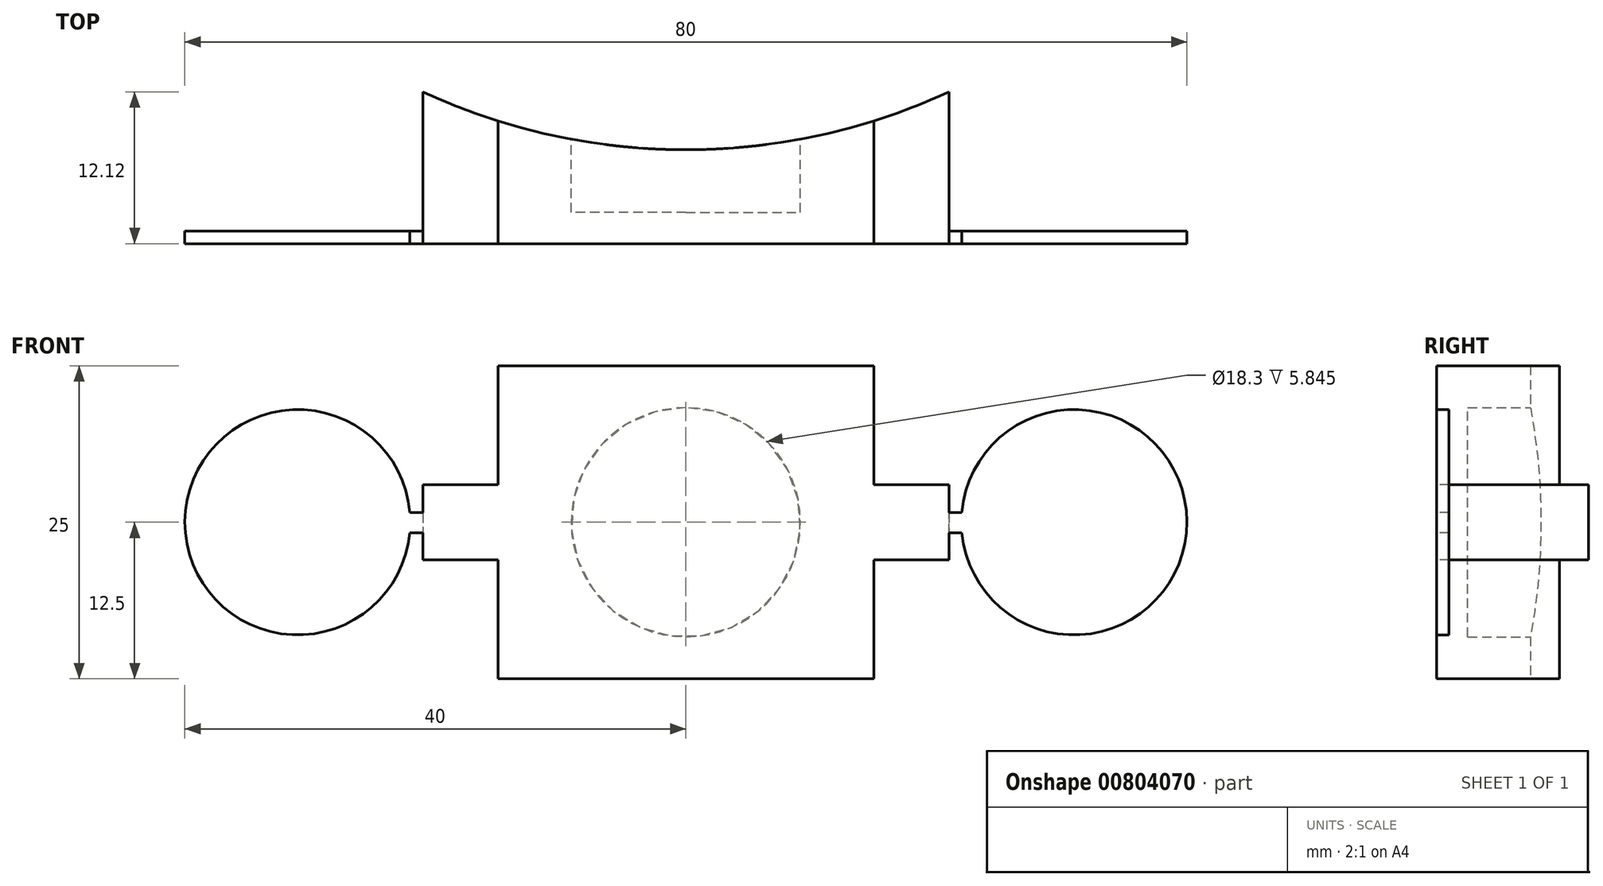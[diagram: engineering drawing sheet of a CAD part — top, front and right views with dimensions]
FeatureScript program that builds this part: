
annotation { "Feature Type Name" : "Feature", "Feature Type Description" : "" }
export const myFeature = defineFeature(function(context is Context, id is Id, definition is map)
    precondition{}
    {
        {
            var Q0;
            Q0=qCreatedBy(makeId("Top.planeOp"),FACE);
            var sketch = newSketch(context, id + "F0", { "sketchPlane" : qUnion([Q0])});
            skArc(sketch, "E0", {"start": v(-50, 0) * mm, "mid": v(0, -50) * mm, "end": v(50, 0) * mm});
            skArc(sketch, "E1", {"start": v(-55, 0) * mm, "mid": v(0, -55) * mm, "end": v(55, 0) * mm});
            skLineSegment(sketch, "E2", {"start": v(-55, 0) * mm, "end": v(-50, 0) * mm});
            skLineSegment(sketch, "E3.trimOffspring", {"start": v(50, 0) * mm, "end": v(55, 0) * mm});
            skSolve(sketch);
        }
        {
            var Q0;
            Q0=qSketchRegion(id+"F0",true);
            extrude(context, id + "F1", {"entities" : qUnion([Q0]), "endBound" : BoundingType.SYMMETRIC, "depth" : 25 * mm, "offsetDistance" : 25 * mm});
        }
        {
            var Q0;
            Q0=makeQuery(id+"F1.opExtrude","CAP_FACE",FACE,{"disambiguationData":[OSD([sQuery(id+"F0.wireOp",EDGE,"E0"),sQuery(id+"F0.wireOp",EDGE,"E1")])],"isStart":false});
            var sketch = newSketch(context, id + "F2", { "sketchPlane" : qUnion([Q0])});
            skLineSegment(sketch, "E4", {"start": v(-55, 0) * mm, "end": v(-55, -57.5) * mm});
            skLineSegment(sketch, "E5", {"start": v(55, 0) * mm, "end": v(55, -57.5) * mm});
            skLineSegment(sketch, "E6", {"start": v(0, -57.5) * mm, "end": v(55, -57.5) * mm});
            skLineSegment(sketch, "E7", {"start": v(0, -57.5) * mm, "end": v(-55, -57.5) * mm});
            skArc(sketch, "E8", {"start": v(-55, 0) * mm, "mid": v(0, -55) * mm, "end": v(55, 0) * mm});
            skLineSegment(sketch, "E9", {"start": v(0, -55) * mm, "end": v(0, -57.5) * mm, "construction": true});
            skSolve(sketch);
        }
        {
            var Q0;
            Q0=qSketchRegion(id+"F2",true);
            extrude(context, id + "F3", {"entities" : qUnion([Q0]), "operationType" : NewBodyOperationType.ADD, "oppositeDirection" : true, "depth" : 25 * mm, "offsetDistance" : 25 * mm});
        }
        {
            var Q0;
            Q0=qCreatedBy(makeId("Front.planeOp"),FACE);
            var sketch = newSketch(context, id + "F4", { "sketchPlane" : qUnion([Q0])});
            skCircle(sketch, "E10", {"center": v(0, 0) * mm, "radius": 9.15 * mm});
            skSolve(sketch);
        }
        {
            var Q0;
            Q0=qSketchRegion(id+"F4",true);
            extrude(context, id + "F5", {"entities" : qUnion([Q0]), "operationType" : NewBodyOperationType.REMOVE, "depth" : 55 * mm, "offsetDistance" : 25 * mm});
        }
        {
            var Q0;
            Q0=qCreatedBy(makeId("Right.planeOp"),FACE);
            var sketch = newSketch(context, id + "F6", { "sketchPlane" : qUnion([Q0])});
            skLineSegment(sketch, "E11", {"start": v(0, 0) * mm, "end": v(-11, 0) * mm, "construction": true});
            skCircle(sketch, "E12", {"center": v(-11, 0) * mm, "radius": 9.05 * mm});
            skSolve(sketch);
        }
        {
            var Q0;
            Q0=qSketchRegion(id+"F6",true);
            extrude(context, id + "F7", {"entities" : qUnion([Q0]), "operationType" : NewBodyOperationType.REMOVE, "endBound" : BoundingType.SYMMETRIC, "oppositeDirection" : true, "depth" : 105 * mm, "offsetDistance" : 25 * mm});
        }
        {
            var Q0;
            Q0=makeQuery(id+"F3.opExtrude","SWEPT_FACE",FACE,{"disambiguationData":[OSD([sQuery(id+"F2.wireOp",EDGE,"E6"),sQuery(id+"F2.wireOp",EDGE,"E7")])]});
            var sketch = newSketch(context, id + "F8", { "sketchPlane" : qUnion([Q0])});
            skLineSegment(sketch, "E13", {"start": v(55, 0) * mm, "end": v(65, 0) * mm, "construction": true});
            skLineSegment(sketch, "E14", {"start": v(-55, 0) * mm, "end": v(-65, 0) * mm, "construction": true});
            skArc(sketch, "E15", {"start": v(56.19, -1.83) * mm, "mid": v(74, 0.24) * mm, "end": v(56.1, 1.35) * mm});
            skArc(sketch, "E16", {"start": v(-56.02, 0.59) * mm, "mid": v(-74, -0.07) * mm, "end": v(-56.01, -0.44) * mm});
            skLineSegment(sketch, "E17", {"start": v(0, -12.5) * mm, "end": v(-55, -12.5) * mm, "construction": true});
            skLineSegment(sketch, "E18", {"start": v(-27.5, -12.5) * mm, "end": v(-27.5, -22.5) * mm, "construction": true});
            skLineSegment(sketch, "E19", {"start": v(0, -12.5) * mm, "end": v(55, -12.5) * mm, "construction": true});
            skLineSegment(sketch, "E20", {"start": v(27.5, -12.5) * mm, "end": v(27.5, -22.5) * mm, "construction": true});
            skLineSegment(sketch, "E21", {"start": v(-55, 12.5) * mm, "end": v(0, 12.5) * mm, "construction": true});
            skLineSegment(sketch, "E22", {"start": v(-27.5, 12.5) * mm, "end": v(-27.5, 22.5) * mm, "construction": true});
            skLineSegment(sketch, "E23", {"start": v(0, 12.5) * mm, "end": v(55, 12.5) * mm, "construction": true});
            skLineSegment(sketch, "E24", {"start": v(27.5, 12.5) * mm, "end": v(27.5, 22.5) * mm, "construction": true});
            skArc(sketch, "E25", {"start": v(26.67, -13.54) * mm, "mid": v(27.5, -31.5) * mm, "end": v(28.35, -13.54) * mm});
            skArc(sketch, "E26", {"start": v(-28.3, -13.54) * mm, "mid": v(-27.52, -31.5) * mm, "end": v(-26.66, -13.54) * mm});
            skArc(sketch, "E27", {"start": v(-26.33, 13.58) * mm, "mid": v(-27.67, 31.5) * mm, "end": v(-28.34, 13.54) * mm});
            skArc(sketch, "E28", {"start": v(28.64, 13.57) * mm, "mid": v(27.37, 31.5) * mm, "end": v(26.62, 13.54) * mm});
            skLineSegment(sketch, "E29", {"start": v(56.19, -1.83) * mm, "end": v(55, -1.83) * mm});
            skLineSegment(sketch, "E30", {"start": v(56.1, 1.35) * mm, "end": v(55, 1.35) * mm});
            skLineSegment(sketch, "E31", {"start": v(55, -1.83) * mm, "end": v(55, 1.35) * mm});
            skLineSegment(sketch, "E32", {"start": v(26.62, 13.54) * mm, "end": v(26.62, 12.5) * mm});
            skLineSegment(sketch, "E33", {"start": v(28.64, 13.57) * mm, "end": v(28.64, 12.5) * mm});
            skLineSegment(sketch, "E34", {"start": v(28.64, 12.5) * mm, "end": v(26.62, 12.5) * mm});
            skLineSegment(sketch, "E35", {"start": v(-28.34, 13.54) * mm, "end": v(-28.34, 12.5) * mm});
            skLineSegment(sketch, "E36", {"start": v(-26.33, 13.58) * mm, "end": v(-26.33, 12.5) * mm});
            skLineSegment(sketch, "E37", {"start": v(-26.33, 12.5) * mm, "end": v(-28.34, 12.5) * mm});
            skLineSegment(sketch, "E38", {"start": v(-56.02, 0.59) * mm, "end": v(-55, 0.59) * mm});
            skLineSegment(sketch, "E39", {"start": v(-56.01, -0.44) * mm, "end": v(-55, -0.44) * mm});
            skLineSegment(sketch, "E40", {"start": v(-55, -0.44) * mm, "end": v(-55, 0.59) * mm});
            skLineSegment(sketch, "E41", {"start": v(-28.3, -13.54) * mm, "end": v(-28.3, -12.5) * mm});
            skLineSegment(sketch, "E42", {"start": v(-26.66, -13.54) * mm, "end": v(-26.66, -12.5) * mm});
            skLineSegment(sketch, "E43", {"start": v(-26.66, -12.5) * mm, "end": v(-28.3, -12.5) * mm});
            skLineSegment(sketch, "E44", {"start": v(26.67, -13.54) * mm, "end": v(26.67, -12.5) * mm});
            skLineSegment(sketch, "E45", {"start": v(28.35, -13.54) * mm, "end": v(28.35, -12.5) * mm});
            skLineSegment(sketch, "E46", {"start": v(28.35, -12.5) * mm, "end": v(26.67, -12.5) * mm});
            skSolve(sketch);
        }
        {
            var Q0;
            Q0=qSketchRegion(id+"F8",true);
            extrude(context, id + "F9", {"entities" : qUnion([Q0]), "operationType" : NewBodyOperationType.ADD, "oppositeDirection" : true, "depth" : 3 * mm, "offsetDistance" : 25 * mm});
        }
        {
            var Q0;
            Q0=makeQuery(id+"F9.boolean.opBoolean","MERGE",FACE,{"derivedFrom":[makeQuery(id+"F3.opExtrude","SWEPT_FACE",FACE,{"disambiguationData":[OSD([sQuery(id+"F2.wireOp",EDGE,"E6"),sQuery(id+"F2.wireOp",EDGE,"E7")])]}),makeQuery(id+"F9.opExtrude","CAP_FACE",FACE,{"disambiguationData":[OSD([sQuery(id+"F8.wireOp",EDGE,"E15"),sQuery(id+"F8.wireOp",EDGE,"E29"),sQuery(id+"F8.wireOp",EDGE,"E30"),sQuery(id+"F8.wireOp",EDGE,"E31")])],"isStart":true}),makeQuery(id+"F9.opExtrude","CAP_FACE",FACE,{"disambiguationData":[OSD([sQuery(id+"F8.wireOp",EDGE,"E16"),sQuery(id+"F8.wireOp",EDGE,"E38"),sQuery(id+"F8.wireOp",EDGE,"E39"),sQuery(id+"F8.wireOp",EDGE,"E40")])],"isStart":true}),makeQuery(id+"F9.opExtrude","CAP_FACE",FACE,{"disambiguationData":[OSD([sQuery(id+"F8.wireOp",EDGE,"E25"),sQuery(id+"F8.wireOp",EDGE,"E44"),sQuery(id+"F8.wireOp",EDGE,"E45"),sQuery(id+"F8.wireOp",EDGE,"E46")])],"isStart":true}),makeQuery(id+"F9.opExtrude","CAP_FACE",FACE,{"disambiguationData":[OSD([sQuery(id+"F8.wireOp",EDGE,"E26"),sQuery(id+"F8.wireOp",EDGE,"E41"),sQuery(id+"F8.wireOp",EDGE,"E42"),sQuery(id+"F8.wireOp",EDGE,"E43")])],"isStart":true}),makeQuery(id+"F9.opExtrude","CAP_FACE",FACE,{"disambiguationData":[OSD([sQuery(id+"F8.wireOp",EDGE,"E27"),sQuery(id+"F8.wireOp",EDGE,"E35"),sQuery(id+"F8.wireOp",EDGE,"E36"),sQuery(id+"F8.wireOp",EDGE,"E37")])],"isStart":true}),makeQuery(id+"F9.opExtrude","CAP_FACE",FACE,{"disambiguationData":[OSD([sQuery(id+"F8.wireOp",EDGE,"E28"),sQuery(id+"F8.wireOp",EDGE,"E32"),sQuery(id+"F8.wireOp",EDGE,"E33"),sQuery(id+"F8.wireOp",EDGE,"E34")])],"isStart":true})]});
            var sketch = newSketch(context, id + "F10", { "sketchPlane" : qUnion([Q0])});
            skLineSegment(sketch, "E47", {"start": v(0, 12.5) * mm, "end": v(0, -12.5) * mm, "construction": true});
            skLineSegment(sketch, "E48.left", {"start": v(-15, 12.5) * mm, "end": v(-15, 3) * mm});
            skLineSegment(sketch, "E48.right", {"start": v(15, 12.5) * mm, "end": v(15, 3) * mm});
            skLineSegment(sketch, "E49", {"start": v(15, 0) * mm, "end": v(0, 0) * mm, "construction": true});
            skLineSegment(sketch, "E50", {"start": v(0, 0) * mm, "end": v(-15, 0) * mm, "construction": true});
            skLineSegment(sketch, "E51", {"start": v(-15, 0) * mm, "end": v(-21, 0) * mm, "construction": true});
            skLineSegment(sketch, "E52", {"start": v(-21, 0) * mm, "end": v(-21, 3) * mm});
            skLineSegment(sketch, "E53", {"start": v(-21, 3) * mm, "end": v(-15, 3) * mm});
            skLineSegment(sketch, "E54", {"start": v(-21, 0) * mm, "end": v(-21, -3) * mm});
            skLineSegment(sketch, "E55", {"start": v(-21, -3) * mm, "end": v(-15, -3) * mm});
            skLineSegment(sketch, "E56.trimOffspring", {"start": v(-15, -3) * mm, "end": v(-15, -12.5) * mm});
            skLineSegment(sketch, "E57", {"start": v(15, 0) * mm, "end": v(21, 0) * mm, "construction": true});
            skLineSegment(sketch, "E58", {"start": v(21, 0) * mm, "end": v(21, 3) * mm});
            skLineSegment(sketch, "E59", {"start": v(21, 3) * mm, "end": v(15, 3) * mm});
            skLineSegment(sketch, "E60", {"start": v(21, 0) * mm, "end": v(21, -3) * mm});
            skLineSegment(sketch, "E61", {"start": v(21, -3) * mm, "end": v(15, -3) * mm});
            skLineSegment(sketch, "E62.trimOffspring", {"start": v(15, -3) * mm, "end": v(15, -12.5) * mm});
            skLineSegment(sketch, "E63", {"start": v(15, 12.5) * mm, "end": v(15, 42.1) * mm});
            skLineSegment(sketch, "E64", {"start": v(15, 42.1) * mm, "end": v(79.78, 42.1) * mm});
            skLineSegment(sketch, "E65", {"start": v(79.78, 42.1) * mm, "end": v(79.78, -47.12) * mm});
            skLineSegment(sketch, "E66", {"start": v(79.78, -47.12) * mm, "end": v(15, -47.12) * mm});
            skLineSegment(sketch, "E67", {"start": v(15, -47.12) * mm, "end": v(15, -12.5) * mm});
            skLineSegment(sketch, "E68", {"start": v(-15, 12.5) * mm, "end": v(-15, 43.2) * mm});
            skLineSegment(sketch, "E69", {"start": v(-15, 43.2) * mm, "end": v(-80.15, 43.2) * mm});
            skLineSegment(sketch, "E70", {"start": v(-80.15, 43.2) * mm, "end": v(-80.15, -41.9) * mm});
            skLineSegment(sketch, "E71", {"start": v(-80.15, -41.9) * mm, "end": v(-15, -41.9) * mm});
            skLineSegment(sketch, "E72", {"start": v(-15, -41.9) * mm, "end": v(-15, -12.5) * mm});
            skSolve(sketch);
        }
        {
            var Q0;
            Q0 = qSketchRegion(id + "F10", true);
            extrude(context, id + "F11", {"entities" : qUnion([Q0]), "operationType" : NewBodyOperationType.REMOVE, "endBound" : BoundingType.THROUGH_ALL, "oppositeDirection" : true, "depth" : 25 * mm, "offsetDistance" : 25 * mm});
        }
        {
            var Q0;
            Q0=makeQuery(id+"F9.boolean.opBoolean","MERGE",FACE,{"derivedFrom":[makeQuery(id+"F3.opExtrude","SWEPT_FACE",FACE,{"disambiguationData":[OSD([sQuery(id+"F2.wireOp",EDGE,"E6"),sQuery(id+"F2.wireOp",EDGE,"E7")])]}),makeQuery(id+"F9.opExtrude","CAP_FACE",FACE,{"disambiguationData":[OSD([sQuery(id+"F8.wireOp",EDGE,"E15"),sQuery(id+"F8.wireOp",EDGE,"E29"),sQuery(id+"F8.wireOp",EDGE,"E30"),sQuery(id+"F8.wireOp",EDGE,"E31")])],"isStart":true}),makeQuery(id+"F9.opExtrude","CAP_FACE",FACE,{"disambiguationData":[OSD([sQuery(id+"F8.wireOp",EDGE,"E16"),sQuery(id+"F8.wireOp",EDGE,"E38"),sQuery(id+"F8.wireOp",EDGE,"E39"),sQuery(id+"F8.wireOp",EDGE,"E40")])],"isStart":true}),makeQuery(id+"F9.opExtrude","CAP_FACE",FACE,{"disambiguationData":[OSD([sQuery(id+"F8.wireOp",EDGE,"E25"),sQuery(id+"F8.wireOp",EDGE,"E44"),sQuery(id+"F8.wireOp",EDGE,"E45"),sQuery(id+"F8.wireOp",EDGE,"E46")])],"isStart":true}),makeQuery(id+"F9.opExtrude","CAP_FACE",FACE,{"disambiguationData":[OSD([sQuery(id+"F8.wireOp",EDGE,"E26"),sQuery(id+"F8.wireOp",EDGE,"E41"),sQuery(id+"F8.wireOp",EDGE,"E42"),sQuery(id+"F8.wireOp",EDGE,"E43")])],"isStart":true}),makeQuery(id+"F9.opExtrude","CAP_FACE",FACE,{"disambiguationData":[OSD([sQuery(id+"F8.wireOp",EDGE,"E27"),sQuery(id+"F8.wireOp",EDGE,"E35"),sQuery(id+"F8.wireOp",EDGE,"E36"),sQuery(id+"F8.wireOp",EDGE,"E37")])],"isStart":true}),makeQuery(id+"F9.opExtrude","CAP_FACE",FACE,{"disambiguationData":[OSD([sQuery(id+"F8.wireOp",EDGE,"E28"),sQuery(id+"F8.wireOp",EDGE,"E32"),sQuery(id+"F8.wireOp",EDGE,"E33"),sQuery(id+"F8.wireOp",EDGE,"E34")])],"isStart":true})]});
            var sketch = newSketch(context, id + "F12", { "sketchPlane" : qUnion([Q0])});
            skLineSegment(sketch, "E73", {"start": v(21, 0) * mm, "end": v(31, 0) * mm, "construction": true});
            skLineSegment(sketch, "E74", {"start": v(-21, 0) * mm, "end": v(-31, 0) * mm, "construction": true});
            skArc(sketch, "E75", {"start": v(-22.03, 0.79) * mm, "mid": v(-40, 0.03) * mm, "end": v(-22.04, -0.85) * mm});
            skArc(sketch, "E76", {"start": v(22.04, -0.86) * mm, "mid": v(40, 0.04) * mm, "end": v(22.03, 0.78) * mm});
            skLineSegment(sketch, "E77", {"start": v(22.03, 0.78) * mm, "end": v(21, 0.78) * mm});
            skLineSegment(sketch, "E78", {"start": v(21, 0.78) * mm, "end": v(21, -0.86) * mm});
            skLineSegment(sketch, "E79", {"start": v(21, -0.86) * mm, "end": v(22.04, -0.86) * mm});
            skLineSegment(sketch, "E80", {"start": v(-22.04, -0.85) * mm, "end": v(-21, -0.85) * mm});
            skLineSegment(sketch, "E81", {"start": v(-21, -0.85) * mm, "end": v(-21, 0.79) * mm});
            skLineSegment(sketch, "E82", {"start": v(-21, 0.79) * mm, "end": v(-22.03, 0.79) * mm});
            skSolve(sketch);
        }
        {
            var Q0;
            Q0 = qSketchRegion(id + "F12", true);
            extrude(context, id + "F13", {"entities" : qUnion([Q0]), "operationType" : NewBodyOperationType.ADD, "oppositeDirection" : true, "depth" : 1 * mm, "offsetDistance" : 25 * mm});
        }
    });
